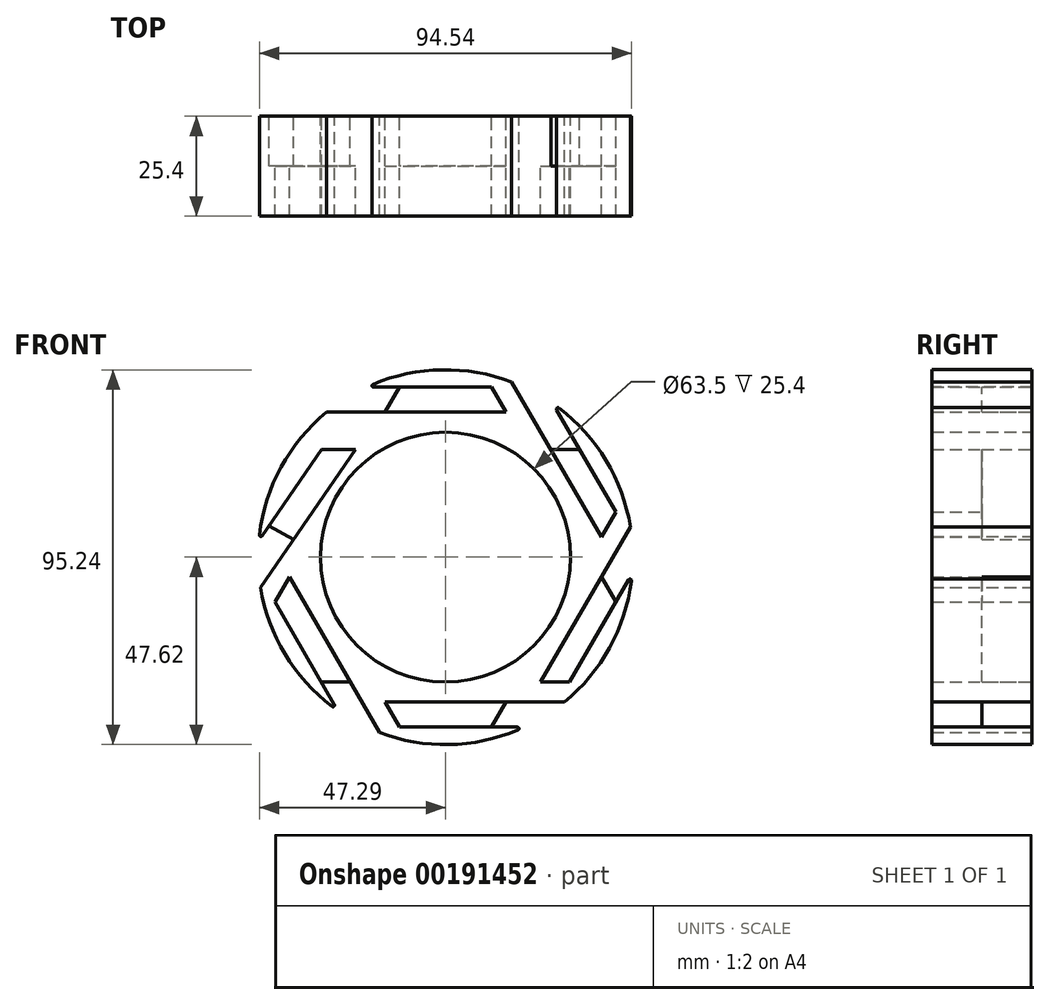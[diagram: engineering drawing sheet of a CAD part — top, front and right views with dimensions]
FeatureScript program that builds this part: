
annotation { "Feature Type Name" : "Feature", "Feature Type Description" : "" }
export const myFeature = defineFeature(function(context is Context, id is Id, definition is map)
    precondition{}
    {
        {
            var Q0;
            Q0=qCreatedBy(makeId("Front.planeOp"),FACE);
            var sketch = newSketch(context, id + "F0", { "sketchPlane" : qUnion([Q0])});
            skCircle(sketch, "E0", {"center": v(0, 0) * mm, "radius": 31.75 * mm});
            skArc(sketch, "E1", {"start": v(30.2, -36.83) * mm, "mid": v(42.1, -22.25) * mm, "end": v(47.44, -4.2) * mm});
            skLineSegment(sketch, "E2", {"start": v(43.26, 11.43) * mm, "end": v(39.6, 5.08) * mm});
            skLineSegment(sketch, "E3", {"start": v(-31.53, 27.3) * mm, "end": v(-22.87, 27.3) * mm});
            skLineSegment(sketch, "E4.trimOffspring", {"start": v(39.6, -5.08) * mm, "end": v(43.26, -11.43) * mm});
            skLineSegment(sketch, "E5.trimOffspring", {"start": v(15.4, 36.83) * mm, "end": v(11.73, 43.18) * mm});
            skLineSegment(sketch, "E6.trimOffspring", {"start": v(26.76, 27.3) * mm, "end": v(34.1, 27.3) * mm});
            skLineSegment(sketch, "E7.trimOffspring", {"start": v(-15.4, 36.83) * mm, "end": v(-11.73, 43.18) * mm});
            skLineSegment(sketch, "E8.trimOffspring", {"start": v(-39.6, -5.08) * mm, "end": v(-43.26, -11.43) * mm});
            skLineSegment(sketch, "E9.trimOffspring", {"start": v(-38.6, 4.45) * mm, "end": v(-44.83, 7.98) * mm});
            skLineSegment(sketch, "E10.trimOffspring", {"start": v(-15.4, -36.83) * mm, "end": v(-11.73, -43.18) * mm});
            skLineSegment(sketch, "E11.trimOffspring", {"start": v(-24.2, -31.75) * mm, "end": v(-31.53, -31.75) * mm});
            skLineSegment(sketch, "E12.trimOffspring", {"start": v(24.2, -31.75) * mm, "end": v(31.53, -31.75) * mm});
            skLineSegment(sketch, "E13.trimOffspring", {"start": v(15.4, -36.83) * mm, "end": v(11.73, -43.18) * mm});
            skPoint(sketch, "E14", {"position": v(-39.6, -5.08) * mm});
            skPoint(sketch, "E15", {"position": v(-43.26, -11.43) * mm});
            skPoint(sketch, "E16", {"position": v(39.6, 5.08) * mm});
            skPoint(sketch, "E17", {"position": v(43.26, 11.43) * mm});
            skPoint(sketch, "E18", {"position": v(11.73, 43.18) * mm});
            skPoint(sketch, "E19", {"position": v(-22.87, 27.3) * mm});
            skPoint(sketch, "E20", {"position": v(-31.53, 27.3) * mm});
            skPoint(sketch, "E21", {"position": v(-15.4, -36.83) * mm});
            skPoint(sketch, "E22", {"position": v(-11.73, -43.18) * mm});
            skPoint(sketch, "E23", {"position": v(24.2, -31.75) * mm});
            skPoint(sketch, "E24", {"position": v(31.53, -31.75) * mm});
            skPoint(sketch, "E25", {"position": v(15.4, 36.83) * mm});
            skLineSegment(sketch, "E26", {"start": v(-15.4, -36.83) * mm, "end": v(30.2, -36.83) * mm});
            skLineSegment(sketch, "E27", {"start": v(-11.73, -43.18) * mm, "end": v(20.1, -43.18) * mm});
            skLineSegment(sketch, "E28", {"start": v(24.2, -31.75) * mm, "end": v(47, 7.73) * mm});
            skLineSegment(sketch, "E29", {"start": v(31.53, -31.75) * mm, "end": v(47.44, -4.2) * mm});
            skArc(sketch, "E30.trimOffspring", {"start": v(47, 7.73) * mm, "mid": v(40.32, 25.34) * mm, "end": v(27.35, 38.99) * mm});
            skLineSegment(sketch, "E31", {"start": v(39.6, 5.08) * mm, "end": v(16.8, 44.56) * mm});
            skLineSegment(sketch, "E32", {"start": v(43.26, 11.43) * mm, "end": v(27.35, 38.99) * mm});
            skArc(sketch, "E33.trimOffspring", {"start": v(16.8, 44.56) * mm, "mid": v(-1.79, 47.6) * mm, "end": v(-20.1, 43.18) * mm});
            skLineSegment(sketch, "E34", {"start": v(15.4, 36.83) * mm, "end": v(-30.2, 36.83) * mm});
            skLineSegment(sketch, "E35", {"start": v(11.73, 43.18) * mm, "end": v(-20.1, 43.18) * mm});
            skArc(sketch, "E36.trimOffspring", {"start": v(-30.2, 36.83) * mm, "mid": v(-42.1, 22.25) * mm, "end": v(-47.44, 4.2) * mm});
            skLineSegment(sketch, "E37", {"start": v(-22.87, 27.3) * mm, "end": v(-47, -7.73) * mm});
            skLineSegment(sketch, "E38", {"start": v(-31.53, 27.3) * mm, "end": v(-47.44, 4.2) * mm});
            skArc(sketch, "E39.trimOffspring", {"start": v(-47, -7.73) * mm, "mid": v(-40.32, -25.34) * mm, "end": v(-27.35, -38.99) * mm});
            skLineSegment(sketch, "E40.trimOffspring", {"start": v(-22.87, 27.3) * mm, "end": v(-31.53, 27.3) * mm});
            skLineSegment(sketch, "E41", {"start": v(-39.6, -5.08) * mm, "end": v(-16.8, -44.56) * mm});
            skLineSegment(sketch, "E42", {"start": v(-43.26, -11.43) * mm, "end": v(-27.35, -38.99) * mm});
            skArc(sketch, "E43.trimOffspring", {"start": v(-16.8, -44.56) * mm, "mid": v(1.79, -47.6) * mm, "end": v(20.1, -43.18) * mm});
            skPoint(sketch, "E44", {"position": v(41.43, 8.25) * mm});
            skLineSegment(sketch, "E45", {"start": v(41.43, 8.25) * mm, "end": v(23.8, 38.78) * mm});
            skPoint(sketch, "E46", {"position": v(30.43, 27.3) * mm});
            skPoint(sketch, "E47", {"position": v(27.93, 31.64) * mm});
            skCircle(sketch, "E48", {"center": v(27.93, 31.64) * mm, "radius": 3.18 * mm});
            skPoint(sketch, "E49", {"position": v(13.56, 40) * mm});
            skPoint(sketch, "E50", {"position": v(-27.2, 27.3) * mm});
            skPoint(sketch, "E51", {"position": v(-41.43, -8.25) * mm});
            skPoint(sketch, "E52", {"position": v(-13.56, -40) * mm});
            skPoint(sketch, "E53", {"position": v(27.86, -31.75) * mm});
            skLineSegment(sketch, "E54", {"start": v(27.86, -31.75) * mm, "end": v(49.2, 5.2) * mm});
            skLineSegment(sketch, "E55", {"start": v(-13.56, -40) * mm, "end": v(32.94, -40) * mm});
            skPoint(sketch, "E55.endSnap0", {"position": v(13.56, -40) * mm});
            skLineSegment(sketch, "E56", {"start": v(-41.43, -8.25) * mm, "end": v(-20.35, -44.77) * mm});
            skLineSegment(sketch, "E57", {"start": v(-27.2, 27.3) * mm, "end": v(-48.7, -3.93) * mm});
            skLineSegment(sketch, "E58", {"start": v(13.56, 40) * mm, "end": v(-21.44, 40) * mm});
            skPoint(sketch, "E58.endSnap0", {"position": v(-13.56, 40) * mm});
            skPoint(sketch, "E59", {"position": v(-13.44, 40) * mm});
            skPoint(sketch, "E60", {"position": v(-44.63, 2) * mm});
            skPoint(sketch, "E61", {"position": v(-25.6, -35.65) * mm});
            skPoint(sketch, "E62", {"position": v(20.63, -40) * mm});
            skPoint(sketch, "E63", {"position": v(43.45, -4.75) * mm});
            skSolve(sketch);
        }
        {
            var Q0;
            Q0=makeQuery(id+"F0.imprint","IMPRINT",FACE,{"disambiguationData":[TD([[makeQuery(id+"F0.imprint","IMPRINT",EDGE,{"derivedFrom":sQuery(id+"F0.wireOp",EDGE,"E0")}),-1.0]])]});
            extrude(context, id + "F1", {"entities" : qUnion([Q0]), "depth" : 25.4 * mm});
        }
        {
            var Q0;
            {var subQ0=sQuery(id+"F0.wireOp",EDGE,"TNsuq5NS-QANT-J0P0-GNbl-TDhvXbvSOdRo");Q0=makeQuery(id+"F0.imprint","IMPRINT",FACE,{"disambiguationData":[TD([[makeQuery(id+"F0.imprint","IMPRINT",EDGE,{"derivedFrom":subQ0}),1.0]])]});}
            var Q1;
            {var subQ0=sQuery(id+"F0.wireOp",EDGE,"ABIK4gMw-uXgZ-muUf-ns2C-MijvyFsJOEyE");Q1=makeQuery(id+"F0.imprint","IMPRINT",FACE,{"disambiguationData":[TD([[makeQuery(id+"F0.imprint","IMPRINT",EDGE,{"derivedFrom":subQ0}),1.0]])]});}
            var Q2;
            {var subQ0=sQuery(id+"F0.wireOp",EDGE,"o0USEca9-N2MO-PAVF-Ghmr-UdLSvRCFERkc");Q2=makeQuery(id+"F0.imprint","IMPRINT",FACE,{"disambiguationData":[TD([[makeQuery(id+"F0.imprint","IMPRINT",EDGE,{"derivedFrom":subQ0}),1.0]])]});}
            var Q3;
            {var subQ0=sQuery(id+"F0.wireOp",EDGE,"heZryI5r-qims-QfQs-cFZ6-yniFHxOi0RHD");Q3=makeQuery(id+"F0.imprint","IMPRINT",FACE,{"disambiguationData":[TD([[makeQuery(id+"F0.imprint","IMPRINT",EDGE,{"derivedFrom":subQ0}),-1.0]])]});}
            var Q4;
            {var subQ0=sQuery(id+"F0.wireOp",EDGE,"YrP4K9g0-3dU6-SZPW-Piva-2CMmqCGKt3cz");Q4=makeQuery(id+"F0.imprint","IMPRINT",FACE,{"disambiguationData":[TD([[makeQuery(id+"F0.imprint","IMPRINT",EDGE,{"derivedFrom":subQ0}),1.0]])]});}
            var Q5;
            {var subQ0=sQuery(id+"F0.wireOp",EDGE,"lwYlyBMg-YqJA-4SKQ-2ayh-eZnohBfo1aWz");Q5=makeQuery(id+"F0.imprint","IMPRINT",FACE,{"disambiguationData":[TD([[makeQuery(id+"F0.imprint","IMPRINT",EDGE,{"derivedFrom":subQ0}),1.0]])]});}
            var Q6;
            {var subQ4=sQuery(id+"F0.wireOp",EDGE,"7JP3Oun1-qaqq-5hJY-S4zt-0LUiuM0NmCbC");Q6=makeQuery(id+"F0.imprint","IMPRINT",FACE,{"disambiguationData":[TD([[makeQuery(id+"F0.imprint","IMPRINT",EDGE,{"derivedFrom":subQ4}),1.0]])]});}
            var Q7;
            {var subQ0=sQuery(id+"F0.wireOp",EDGE,"M9a5kfod-dTNz-iBr0-bDnr-pHYXJr0BWlKe");Q7=makeQuery(id+"F0.imprint","IMPRINT",FACE,{"disambiguationData":[TD([[makeQuery(id+"F0.imprint","IMPRINT",EDGE,{"derivedFrom":subQ0}),-1.0]])]});}
            var Q8;
            {var subQ0=sQuery(id+"F0.wireOp",EDGE,"63fcc126-4580-46d7-a25e-f3c919feebd9.trimOffspring");Q8=makeQuery(id+"F0.imprint","IMPRINT",FACE,{"disambiguationData":[TD([[makeQuery(id+"F0.imprint","IMPRINT",EDGE,{"derivedFrom":subQ0}),1.0]])]});}
            var Q9;
            {var subQ5=sQuery(id+"F0.wireOp",EDGE,"c5ce84b3-573b-4fc1-943b-820cfa6c27b8.trimOffspring");Q9=makeQuery(id+"F0.imprint","IMPRINT",FACE,{"disambiguationData":[TD([[makeQuery(id+"F0.imprint","IMPRINT",EDGE,{"derivedFrom":subQ5}),1.0]])]});}
            var Q10;
            {var subQ5=sQuery(id+"F0.wireOp",EDGE,"32430125-7888-445b-adc1-e5221be84db3.trimOffspring");Q10=makeQuery(id+"F0.imprint","IMPRINT",FACE,{"disambiguationData":[TD([[makeQuery(id+"F0.imprint","IMPRINT",EDGE,{"derivedFrom":subQ5}),1.0]])]});}
            var Q11;
            {var subQ2=sQuery(id+"F0.wireOp",EDGE,"Dxh2Devz-sjd5-BiHN-aqyt-mWFseefKTBmN");Q11=makeQuery(id+"F0.imprint","IMPRINT",FACE,{"disambiguationData":[TD([[makeQuery(id+"F0.imprint","IMPRINT",EDGE,{"derivedFrom":subQ2}),-1.0]])]});}
            var Q12;
            {var subQ0=sQuery(id+"F0.wireOp",EDGE,"E9.trimOffspring");Q12=makeQuery(id+"F0.imprint","IMPRINT",FACE,{"disambiguationData":[TD([[makeQuery(id+"F0.imprint","IMPRINT",EDGE,{"derivedFrom":subQ0}),-1.0]])]});}
            var Q13;
            {var subQ0=sQuery(id+"F0.wireOp",EDGE,"E8.trimOffspring");Q13=makeQuery(id+"F0.imprint","IMPRINT",FACE,{"disambiguationData":[TD([[makeQuery(id+"F0.imprint","IMPRINT",EDGE,{"derivedFrom":subQ0}),1.0]])]});}
            var Q14;
            {var subQ0=sQuery(id+"F0.wireOp",EDGE,"E10.trimOffspring");Q14=makeQuery(id+"F0.imprint","IMPRINT",FACE,{"disambiguationData":[TD([[makeQuery(id+"F0.imprint","IMPRINT",EDGE,{"derivedFrom":subQ0}),1.0]])]});}
            var Q15;
            {var subQ0=sQuery(id+"F0.wireOp",EDGE,"E4.trimOffspring");Q15=makeQuery(id+"F0.imprint","IMPRINT",FACE,{"disambiguationData":[TD([[makeQuery(id+"F0.imprint","IMPRINT",EDGE,{"derivedFrom":subQ0}),-1.0]])]});}
            var Q16;
            {var subQ0=sQuery(id+"F0.wireOp",EDGE,"E2");Q16=makeQuery(id+"F0.imprint","IMPRINT",FACE,{"disambiguationData":[TD([[makeQuery(id+"F0.imprint","IMPRINT",EDGE,{"derivedFrom":subQ0}),-1.0]])]});}
            var Q17;
            {var subQ0=sQuery(id+"F0.wireOp",EDGE,"E5.trimOffspring");Q17=makeQuery(id+"F0.imprint","IMPRINT",FACE,{"disambiguationData":[TD([[makeQuery(id+"F0.imprint","IMPRINT",EDGE,{"derivedFrom":subQ0}),1.0]])]});}
            extrude(context, id + "F2", {"entities" : qUnion([Q0, Q1, Q2, Q3, Q4, Q5, Q6, Q7, Q8, Q9, Q10, Q11, Q12, Q13, Q14, Q15, Q16, Q17]), "operationType" : NewBodyOperationType.ADD, "depth" : 12.7 * mm});
        }
        {
            var Q0;
            Q0=makeQuery(id+"F1.opExtrude","SWEPT_EDGE",EDGE,{"disambiguationData":[OSD([sQuery(id+"F0.wireOp",EDGE,"4708ec58-b6aa-41ac-b138-f8879647f75f.trimOffspring"),sQuery(id+"F0.wireOp",EDGE,"LdhKgMY1-c288-TwdI-4NrZ-i5i1MzOBN5Cy")])]});
            var Q1;
            Q1=makeQuery(id+"F1.opExtrude","SWEPT_EDGE",EDGE,{"disambiguationData":[OSD([sQuery(id+"F0.wireOp",EDGE,"xAAY2lhg-6pBi-ph3d-6AAq-6HJjUXgKlnu2"),sQuery(id+"F0.wireOp",EDGE,"87a6c7e8-256f-42cd-92e7-f0e6a3deef4a.trimOffspring")])]});
            var Q2;
            Q2=makeQuery(id+"F1.opExtrude","SWEPT_EDGE",EDGE,{"disambiguationData":[OSD([sQuery(id+"F0.wireOp",EDGE,"EKKhqvlA-jjb1-W3RU-ilHK-s7FaZldMSCcS"),sQuery(id+"F0.wireOp",EDGE,"343cd82b-8adb-48d5-ac3f-6bcb24874289.trimOffspring")])]});
            var Q3;
            Q3=makeQuery(id+"F1.opExtrude","SWEPT_EDGE",EDGE,{"disambiguationData":[OSD([sQuery(id+"F0.wireOp",EDGE,"ddcAJP5H-NvLt-mhk0-XeYF-IAQGrfGcYmdd"),sQuery(id+"F0.wireOp",EDGE,"b77f6b88-1a06-41b7-ba3a-3b1eb8d71a95.trimOffspring")])]});
            var Q4;
            Q4=makeQuery(id+"F1.opExtrude","SWEPT_EDGE",EDGE,{"disambiguationData":[OSD([sQuery(id+"F0.wireOp",EDGE,"aHCZKm9X-Z7xg-HwkX-8SYc-KivfaWxt6Vj1"),sQuery(id+"F0.wireOp",EDGE,"a1ec96e3-fc72-4263-ab90-4e1a4a2426c8.trimOffspring")])]});
            var Q5;
            Q5=makeQuery(id+"F1.opExtrude","SWEPT_EDGE",EDGE,{"disambiguationData":[OSD([sQuery(id+"F0.wireOp",EDGE,"9LNj1hUI-6n7v-PEWu-DnKH-TXIlcBmHKdEJ"),sQuery(id+"F0.wireOp",EDGE,"F5z4oLuW-ftGP-XFs9-eBst-aHDobwM87423")])]});
            var Q6;
            Q6=makeQuery(id+"F1.opExtrude","SWEPT_EDGE",EDGE,{"disambiguationData":[OSD([sQuery(id+"F0.wireOp",EDGE,"E36.trimOffspring"),sQuery(id+"F0.wireOp",EDGE,"E38")])]});
            var Q7;
            Q7=makeQuery(id+"F1.opExtrude","SWEPT_EDGE",EDGE,{"disambiguationData":[OSD([sQuery(id+"F0.wireOp",EDGE,"E39.trimOffspring"),sQuery(id+"F0.wireOp",EDGE,"E42")])]});
            var Q8;
            Q8=makeQuery(id+"F1.opExtrude","SWEPT_EDGE",EDGE,{"disambiguationData":[OSD([sQuery(id+"F0.wireOp",EDGE,"E27"),sQuery(id+"F0.wireOp",EDGE,"E43.trimOffspring")])]});
            var Q9;
            Q9=makeQuery(id+"F1.opExtrude","SWEPT_EDGE",EDGE,{"disambiguationData":[OSD([sQuery(id+"F0.wireOp",EDGE,"E1"),sQuery(id+"F0.wireOp",EDGE,"E29")])]});
            var Q10;
            Q10=makeQuery(id+"F1.opExtrude","SWEPT_EDGE",EDGE,{"disambiguationData":[OSD([sQuery(id+"F0.wireOp",EDGE,"E30.trimOffspring"),sQuery(id+"F0.wireOp",EDGE,"E32")])]});
            var Q11;
            Q11=makeQuery(id+"F1.opExtrude","SWEPT_EDGE",EDGE,{"disambiguationData":[OSD([sQuery(id+"F0.wireOp",EDGE,"E33.trimOffspring"),sQuery(id+"F0.wireOp",EDGE,"E35")])]});
            fillet(context, id + "F3", {"entities" : qUnion([Q0, Q1, Q2, Q3, Q4, Q5, Q6, Q7, Q8, Q9, Q10, Q11]), "radius" : 0.38 * mm, "tangentPropagation" : true, "allowEdgeOverflow" : false});
        }
    });
